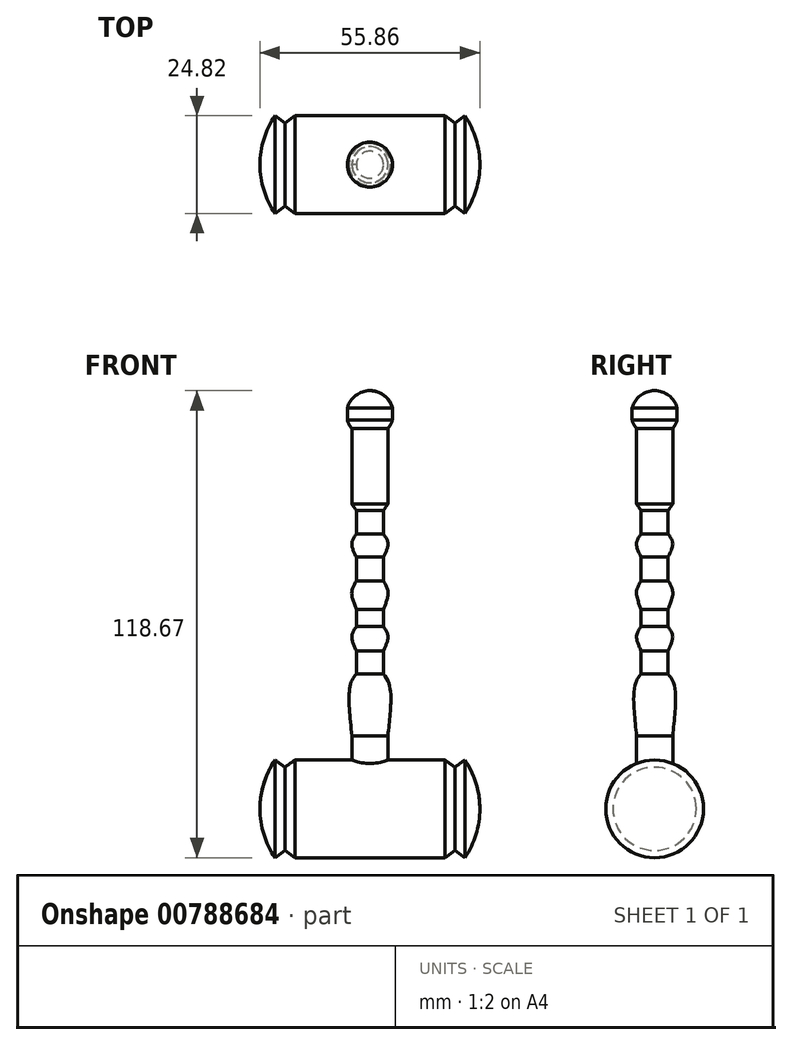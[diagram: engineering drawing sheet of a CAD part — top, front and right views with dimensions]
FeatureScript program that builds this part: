
annotation { "Feature Type Name" : "Feature", "Feature Type Description" : "" }
export const myFeature = defineFeature(function(context is Context, id is Id, definition is map)
    precondition{}
    {
        {
            var Q0;
            Q0=qCreatedBy(makeId("Front.planeOp"),FACE);
            var sketch = newSketch(context, id + "F0", { "sketchPlane" : qUnion([Q0])});
            skArc(sketch, "E0", {"start": v(0, 40.88) * mm, "mid": v(3.6, 42.1) * mm, "end": v(5.72, 45.24) * mm});
            skLineSegment(sketch, "E1", {"start": v(4.6, 43.06) * mm, "end": v(4.6, 23.94) * mm});
            skLineSegment(sketch, "E2", {"start": v(0, 46.8) * mm, "end": v(0, -55.08) * mm, "construction": true});
            skFitSpline(sketch, "E3", {"points": [v(4.6, 23.94) * mm, v(2.07, 18.62) * mm, v(4.6, 13.9) * mm, v(2.27, 7.2) * mm, v(4.6, 1.68) * mm, v(2.84, -5.65) * mm, v(4.6, -9.75) * mm, v(2.27, -16.85) * mm, v(4.6, -20.99) * mm, v(4.6, -34.98) * mm], "startDerivative": vector(-33.1, -51.35) * mm, "endDerivative": vector(-9.8, -103.78) * mm});
            skLineSegment(sketch, "E4", {"start": v(4.6, -34.98) * mm, "end": v(4.6, -45.72) * mm});
            skLineSegment(sketch, "E5", {"start": v(4.6, -45.72) * mm, "end": v(0, -45.72) * mm});
            skLineSegment(sketch, "E6", {"start": v(0, -45.72) * mm, "end": v(0, 40.88) * mm});
            skLineSegment(sketch, "E7", {"start": v(0, 40.88) * mm, "end": v(0, 52.73) * mm});
            skLineSegment(sketch, "E8", {"start": v(3.45, 22.17) * mm, "end": v(3.45, -45.72) * mm});
            skLineSegment(sketch, "E9", {"start": v(5.72, 45.24) * mm, "end": v(5.72, 48.36) * mm});
            skArc(sketch, "E10.trimOffspring", {"start": v(5.72, 48.36) * mm, "mid": v(3.6, 51.52) * mm, "end": v(0, 52.73) * mm});
            skLineSegment(sketch, "E11", {"start": v(3.45, 16.26) * mm, "end": v(3.45, 22.27) * mm});
            skSolve(sketch);
        }
        {
            var Q0;
            Q0 = qSketchRegion(id + "F0", true);
            var Q1;
            Q1=sQuery(id+"F0.wireOp",EDGE,"E6");
            revolve(context, id + "F1", {"surfaceOperationType" : NewSurfaceOperationType.NEW, "entities" : qUnion([Q0]), "axis" : qUnion([Q1]), "revolveType" : RevolveType.FULL});
        }
        {
            var Q0;
            Q0=qCreatedBy(makeId("Front.planeOp"),FACE);
            var sketch = newSketch(context, id + "F2", { "sketchPlane" : qUnion([Q0])});
            skLineSegment(sketch, "E12", {"start": v(0, -41.12) * mm, "end": v(19.05, -41.12) * mm});
            skLineSegment(sketch, "E13", {"start": v(19.05, -41.12) * mm, "end": v(21.6, -42.95) * mm});
            skLineSegment(sketch, "E14", {"start": v(21.6, -42.95) * mm, "end": v(24.11, -41.12) * mm});
            skArc(sketch, "E15", {"start": v(27.93, -53.53) * mm, "mid": v(26.95, -47.04) * mm, "end": v(24.11, -41.12) * mm});
            skLineSegment(sketch, "E16", {"start": v(27.93, -53.53) * mm, "end": v(0, -53.53) * mm});
            skLineSegment(sketch, "E17", {"start": v(0, -53.53) * mm, "end": v(0, -41.12) * mm});
            skLineSegment(sketch, "E18.MirrorCS", {"start": v(0, -41.12) * mm, "end": v(-19.05, -41.12) * mm});
            skLineSegment(sketch, "E19.MirrorCS", {"start": v(-19.05, -41.12) * mm, "end": v(-21.6, -42.95) * mm});
            skLineSegment(sketch, "E20.MirrorCS", {"start": v(-21.6, -42.95) * mm, "end": v(-24.11, -41.12) * mm});
            skArc(sketch, "E21.MirrorCS", {"start": v(-27.93, -53.53) * mm, "mid": v(-26.95, -47.04) * mm, "end": v(-24.11, -41.12) * mm});
            skLineSegment(sketch, "E22.MirrorCS", {"start": v(-27.93, -53.53) * mm, "end": v(0, -53.53) * mm});
            skSolve(sketch);
        }
        {
            var Q0;
            Q0 = qSketchRegion(id + "F2", true);
            var Q1;
            Q1=sQuery(id+"F2.wireOp",EDGE,"E22.MirrorCS");
            revolve(context, id + "F3", {"operationType" : NewBodyOperationType.ADD, "surfaceOperationType" : NewSurfaceOperationType.NEW, "entities" : qUnion([Q0]), "axis" : qUnion([Q1]), "revolveType" : RevolveType.FULL});
        }
    });
